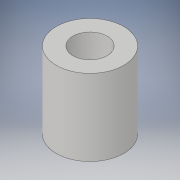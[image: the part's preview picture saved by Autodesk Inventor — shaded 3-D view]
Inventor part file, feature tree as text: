
AUTODESK INVENTOR PART (.ipt)
format: ipt  version: 2017.1 (Build 211199000, 199)  size: 94,208 bytes
history: native  units: in
note: dims shown in document units (in); Inventor stores cm internally (conversion verified against a paired STEP export)
features: extrude x1, sketch x1
ambient origin geometry x8: Origin, YZ Plane, XZ Plane, XY Plane, X Axis, Y Axis, Z Axis, Center Point
bodies: Solid1 (feature_tree)
feature tree (2):
  extrude  "Extrusion1"  Depth=0.85in TaperAngle=0.0deg
  sketch  "Sketch1"  dims[d0=0.75in d1=0.85in d2=0.0in d3=0.38in]
